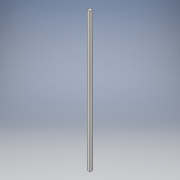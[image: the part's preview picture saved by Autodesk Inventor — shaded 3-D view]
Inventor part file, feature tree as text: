
AUTODESK INVENTOR PART (.ipt)
format: ipt  version: 2017 (Build 210142000, 142)  size: 91,136 bytes
history: native  units: in
note: dims shown in document units (in); Inventor stores cm internally (conversion verified against a paired STEP export)
features: extrude x1, sketch x1
ambient origin geometry x8: Origin, YZ Plane, XZ Plane, XY Plane, X Axis, Y Axis, Z Axis, Center Point
bodies: Solid1 (feature_tree)
feature tree (2):
  extrude  "Extrusion1"  Depth=12.0in
  sketch  "Sketch1"  dims[d0=0.25in d1=12.0in d2=0.25in d3=0.0in]
